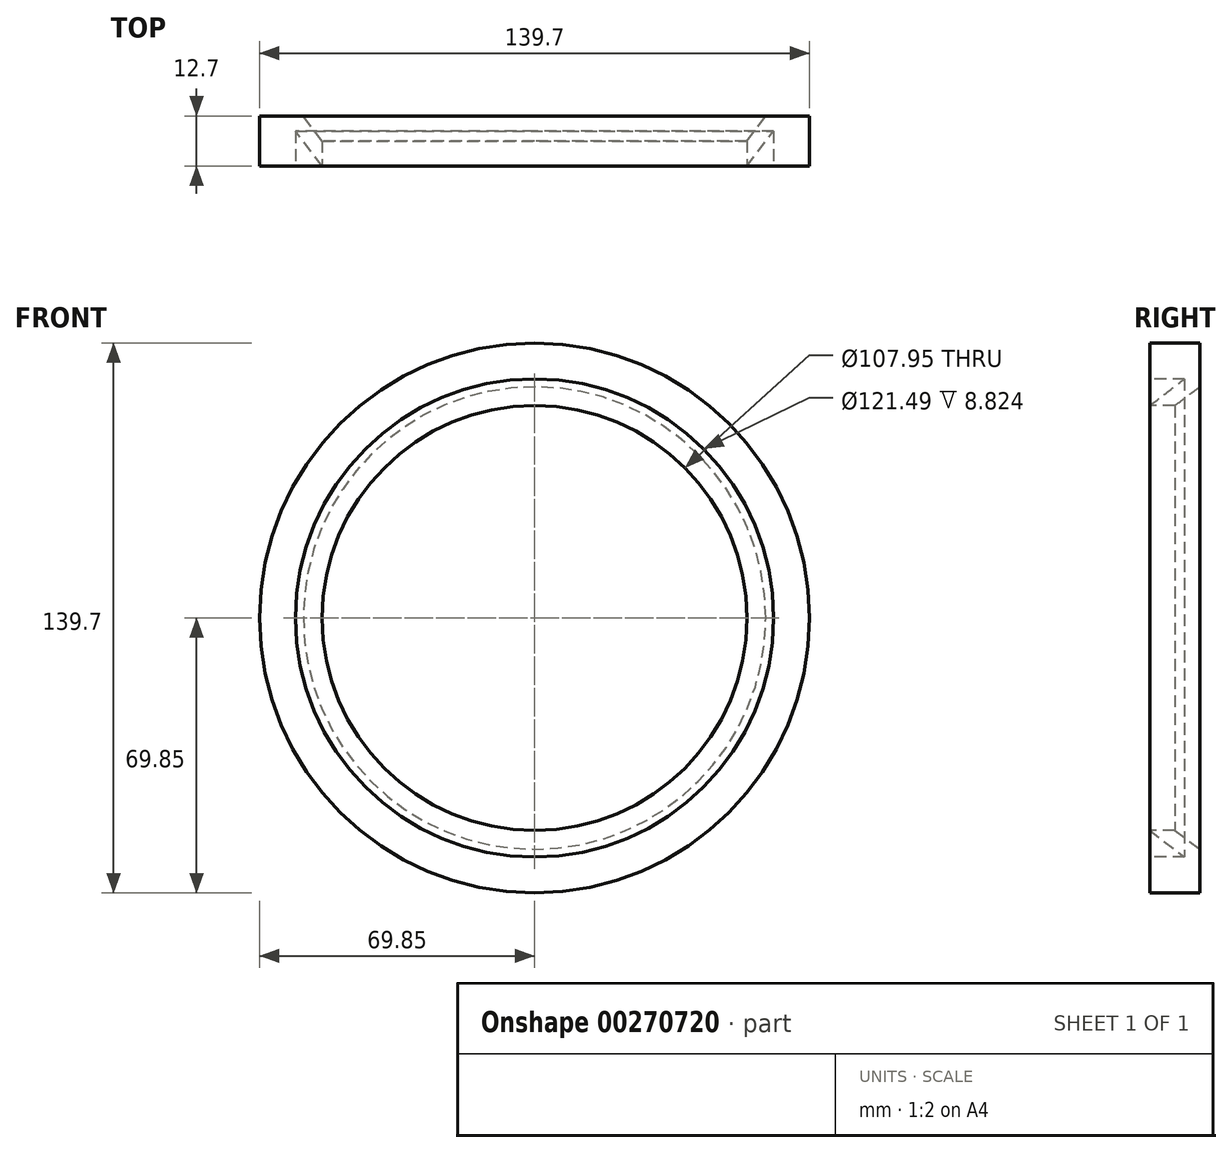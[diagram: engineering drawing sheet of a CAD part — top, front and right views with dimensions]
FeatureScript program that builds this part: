
annotation { "Feature Type Name" : "Feature", "Feature Type Description" : "" }
export const myFeature = defineFeature(function(context is Context, id is Id, definition is map)
    precondition{}
    {
        {
            var Q0;
            Q0=qCreatedBy(makeId("Front.planeOp"),FACE);
            var sketch = newSketch(context, id + "F0", { "sketchPlane" : qUnion([Q0])});
            skCircle(sketch, "E0", {"center": v(0, 0) * mm, "radius": 69.85 * mm});
            skSolve(sketch);
        }
        {
            var Q0;
            Q0=qCreatedBy(makeId("Right.planeOp"),FACE);
            var sketch = newSketch(context, id + "F1", { "sketchPlane" : qUnion([Q0])});
            skLineSegment(sketch, "E1.0", {"start": v(0, -69.85) * mm, "end": v(0, 69.85) * mm, "construction": true});
            skLineSegment(sketch, "E2", {"start": v(-6.35, 69.85) * mm, "end": v(6.35, 69.85) * mm, "construction": true});
            skLineSegment(sketch, "E3", {"start": v(-32.65, 0) * mm, "end": v(26.66, 0) * mm, "construction": true});
            skLineSegment(sketch, "E4.0", {"start": v(-32.65, 53.98) * mm, "end": v(26.66, 53.98) * mm, "construction": true});
            skLineSegment(sketch, "E5", {"start": v(-6.35, 69.85) * mm, "end": v(-6.35, 53.98) * mm, "construction": true});
            skLineSegment(sketch, "E6", {"start": v(6.35, 69.85) * mm, "end": v(6.35, 58.73) * mm});
            skLineSegment(sketch, "E7", {"start": v(6.35, 53.98) * mm, "end": v(-6.35, 53.98) * mm});
            skLineSegment(sketch, "E8", {"start": v(6.35, 69.85) * mm, "end": v(-6.35, 69.85) * mm});
            skLineSegment(sketch, "E9", {"start": v(-6.35, 69.85) * mm, "end": v(-6.35, 60.74) * mm});
            skLineSegment(sketch, "E10", {"start": v(-6.35, 60.74) * mm, "end": v(2.47, 60.74) * mm});
            skLineSegment(sketch, "E11", {"start": v(2.47, 60.74) * mm, "end": v(-6.35, 53.98) * mm});
            skLineSegment(sketch, "E12", {"start": v(6.35, 58.73) * mm, "end": v(0, 53.98) * mm});
            skSolve(sketch);
        }
        {
            var Q0;
            Q0=makeQuery(id+"F1.imprint","IMPRINT",FACE,{"disambiguationData":[TD([[makeQuery(id+"F1.imprint","IMPRINT",EDGE,{"derivedFrom":sQuery(id+"F1.wireOp",EDGE,"E6")}),-1.0]])]});
            var Q1;
            Q1=sQuery(id+"F0.wireOp",EDGE,"E0");
            sweep(context, id + "F2", {"profiles" : qUnion([Q0]), "path" : qUnion([Q1])});
        }
    });
